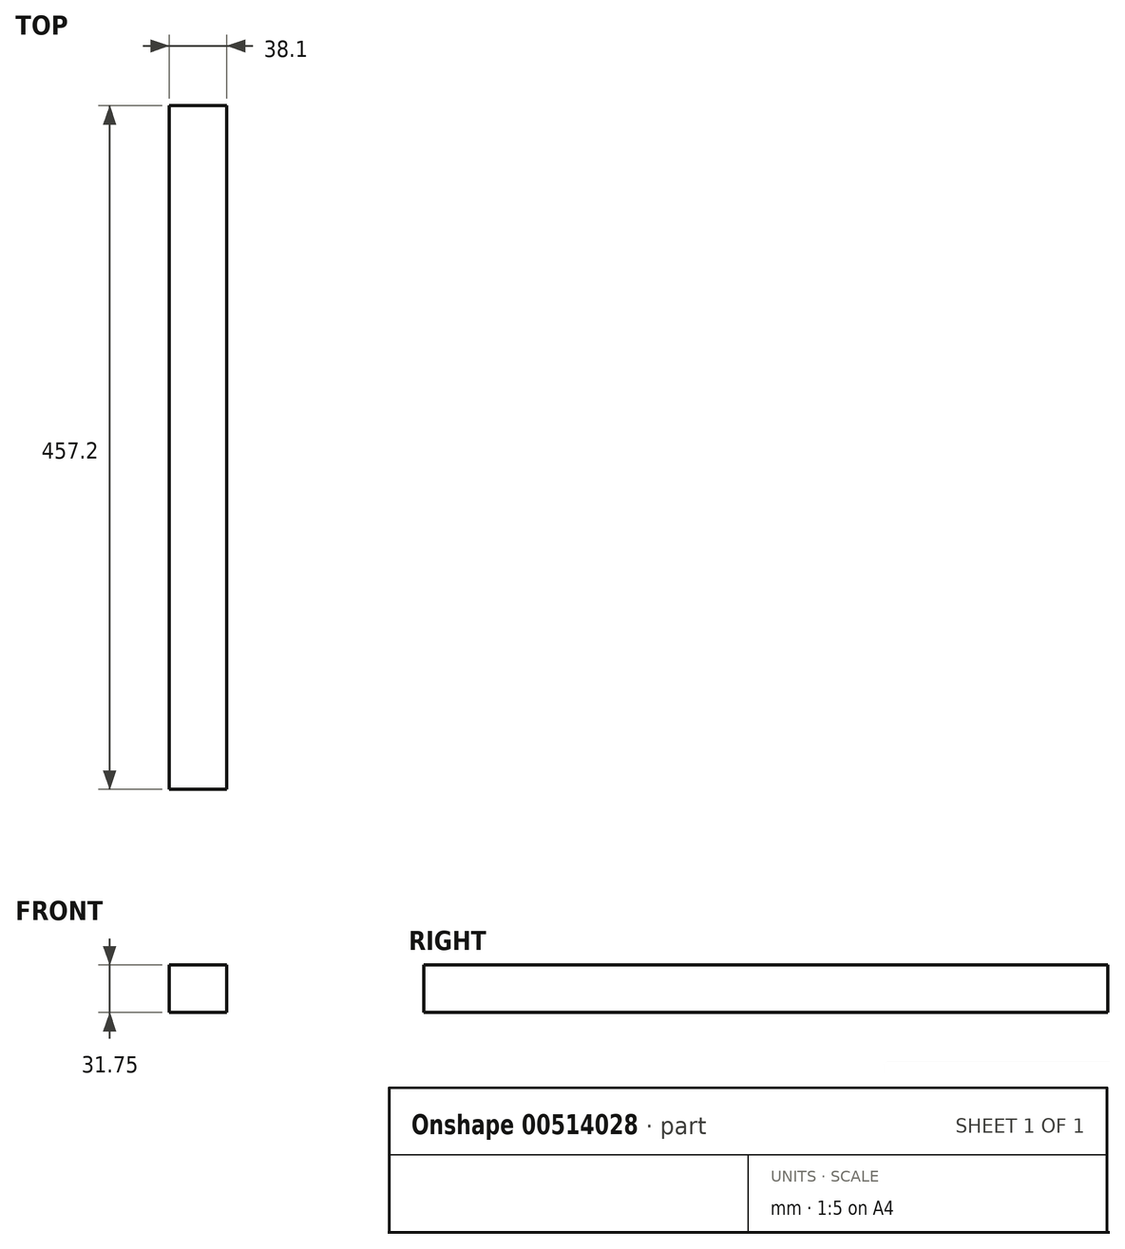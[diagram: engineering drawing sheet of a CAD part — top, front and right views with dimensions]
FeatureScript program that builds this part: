
annotation { "Feature Type Name" : "Feature", "Feature Type Description" : "" }
export const myFeature = defineFeature(function(context is Context, id is Id, definition is map)
    precondition{}
    {
        {
            var Q0;
            Q0=qCreatedBy(makeId("Top.planeOp"),FACE);
            var sketch = newSketch(context, id + "F0", { "sketchPlane" : qUnion([Q0])});
            skLineSegment(sketch, "E0.bottom", {"start": v(-21.43, 231.2) * mm, "end": v(16.67, 231.2) * mm});
            skLineSegment(sketch, "E0.top", {"start": v(-21.43, -226) * mm, "end": v(16.67, -226) * mm});
            skLineSegment(sketch, "E0.left", {"start": v(-21.43, 231.2) * mm, "end": v(-21.43, -226) * mm});
            skLineSegment(sketch, "E0.right", {"start": v(16.67, 231.2) * mm, "end": v(16.67, -226) * mm});
            skSolve(sketch);
        }
        {
            var Q0;
            Q0=makeQuery(id+"F0.imprint","IMPRINT",FACE,{"disambiguationData":[TD([[makeQuery(id+"F0.imprint","IMPRINT",EDGE,{"derivedFrom":sQuery(id+"F0.wireOp",EDGE,"E0.bottom")}),-1.0]])]});
            extrude(context, id + "F1", {"entities" : qUnion([Q0]), "depth" : 31.75 * mm, "offsetDistance" : 25.4 * mm});
        }
    });
